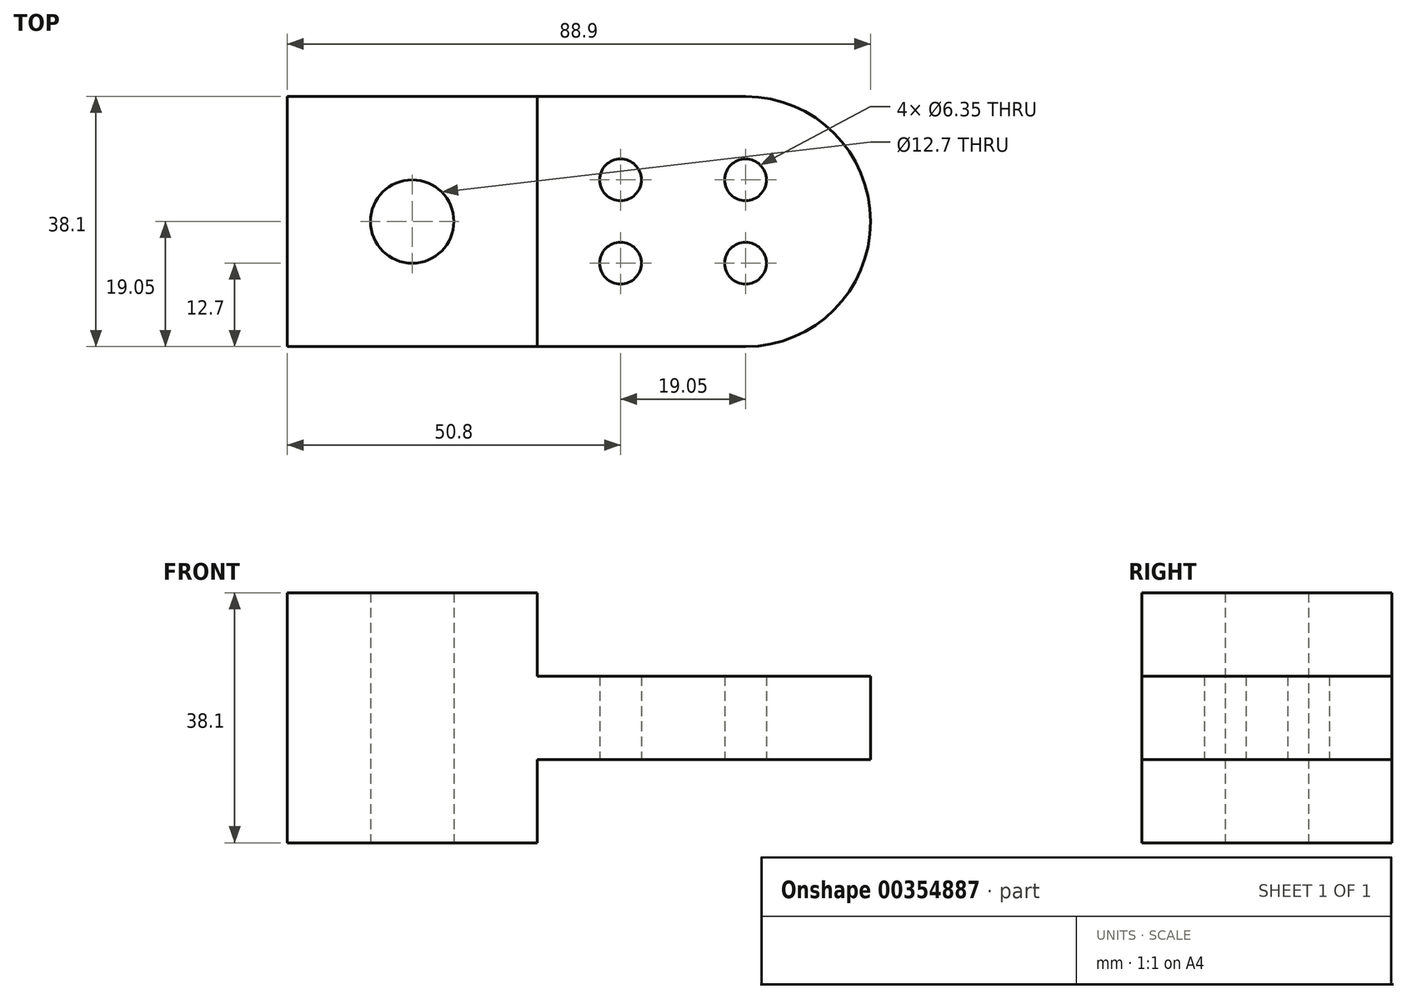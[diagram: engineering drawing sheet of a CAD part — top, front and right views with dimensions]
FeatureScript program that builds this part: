
annotation { "Feature Type Name" : "Feature", "Feature Type Description" : "" }
export const myFeature = defineFeature(function(context is Context, id is Id, definition is map)
    precondition{}
    {
        {
            var Q0;
            Q0=qCreatedBy(makeId("Top.planeOp"),FACE);
            var sketch = newSketch(context, id + "F0", { "sketchPlane" : qUnion([Q0])});
            skLineSegment(sketch, "E0.bottom", {"start": v(-38.1, 19.05) * mm, "end": v(0, 19.05) * mm});
            skLineSegment(sketch, "E0.top", {"start": v(-38.1, -19.05) * mm, "end": v(0, -19.05) * mm});
            skLineSegment(sketch, "E0.left", {"start": v(-38.1, 19.05) * mm, "end": v(-38.1, -19.05) * mm});
            skLineSegment(sketch, "E0.right", {"start": v(0, 19.05) * mm, "end": v(0, -19.05) * mm});
            skArc(sketch, "E1", {"start": v(31.75, -19.05) * mm, "mid": v(50.8, 0) * mm, "end": v(31.75, 19.05) * mm});
            skLineSegment(sketch, "E2", {"start": v(0, 19.05) * mm, "end": v(31.75, 19.05) * mm});
            skLineSegment(sketch, "E3", {"start": v(31.75, -19.05) * mm, "end": v(0, -19.05) * mm});
            skCircle(sketch, "E4", {"center": v(-19.05, 0) * mm, "radius": 6.35 * mm});
            skCircle(sketch, "E5", {"center": v(12.7, 6.35) * mm, "radius": 3.18 * mm});
            skCircle(sketch, "E6", {"center": v(31.75, 6.35) * mm, "radius": 3.18 * mm});
            skCircle(sketch, "E7", {"center": v(31.75, -6.35) * mm, "radius": 3.18 * mm});
            skCircle(sketch, "E8", {"center": v(12.7, -6.35) * mm, "radius": 3.18 * mm});
            skLineSegment(sketch, "E9", {"start": v(12.7, -6.35) * mm, "end": v(55.6, -6.35) * mm, "construction": true});
            skLineSegment(sketch, "E10", {"start": v(12.7, 6.35) * mm, "end": v(54.03, 6.35) * mm, "construction": true});
            skLineSegment(sketch, "E11", {"start": v(12.7, 6.35) * mm, "end": v(12.7, -6.35) * mm, "construction": true});
            skLineSegment(sketch, "E12", {"start": v(31.75, 6.35) * mm, "end": v(31.75, -6.35) * mm, "construction": true});
            skSolve(sketch);
        }
        {
            var Q0;
            Q0=makeQuery(id+"F0.imprint","IMPRINT",FACE,{"disambiguationData":[TD([[makeQuery(id+"F0.imprint","IMPRINT",EDGE,{"derivedFrom":sQuery(id+"F0.wireOp",EDGE,"E0.bottom")}),-1.0]])]});
            extrude(context, id + "F1", {"entities" : qUnion([Q0]), "depth" : 38.1 * mm, "symmetric" : true});
        }
        {
            var Q0;
            Q0=makeQuery(id+"F0.imprint","IMPRINT",FACE,{"disambiguationData":[TD([[makeQuery(id+"F0.imprint","IMPRINT",EDGE,{"derivedFrom":sQuery(id+"F0.wireOp",EDGE,"E0.right")}),1.0]])]});
            extrude(context, id + "F2", {"entities" : qUnion([Q0]), "operationType" : NewBodyOperationType.ADD, "depth" : 12.7 * mm, "symmetric" : true});
        }
    });
